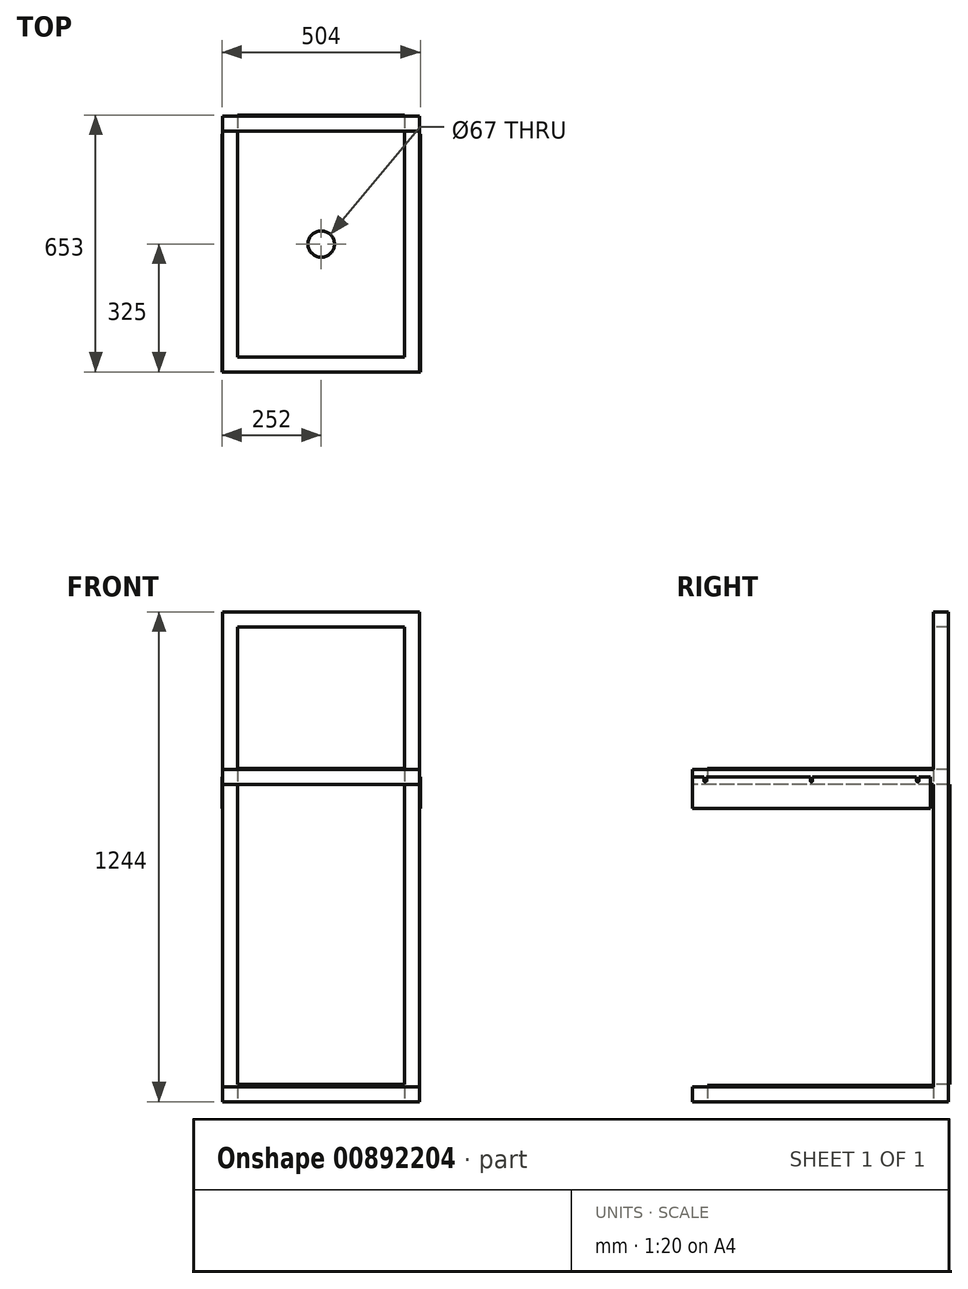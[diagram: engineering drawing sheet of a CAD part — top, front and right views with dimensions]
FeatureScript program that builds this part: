
annotation { "Feature Type Name" : "Feature", "Feature Type Description" : "" }
export const myFeature = defineFeature(function(context is Context, id is Id, definition is map)
    precondition{}
    {
        {
            var Q0;
            Q0=qCreatedBy(makeId("Front.planeOp"),FACE);
            var sketch = newSketch(context, id + "F0", { "sketchPlane" : qUnion([Q0])});
            skLineSegment(sketch, "E0.bottom", {"start": v(0, 0) * mm, "end": v(-500, 0) * mm});
            skLineSegment(sketch, "E0.top", {"start": v(0, 38) * mm, "end": v(-500, 38) * mm});
            skLineSegment(sketch, "E0.left", {"start": v(0, 0) * mm, "end": v(0, 38) * mm});
            skLineSegment(sketch, "E0.right", {"start": v(-500, 0) * mm, "end": v(-500, 38) * mm});
            skSolve(sketch);
        }
        {
            var Q0;
            Q0=makeQuery(id+"F0.imprint","IMPRINT",FACE,{"disambiguationData":[TD([[makeQuery(id+"F0.imprint","IMPRINT",EDGE,{"derivedFrom":sQuery(id+"F0.wireOp",EDGE,"E0.bottom")}),-1.0]])]});
            extrude(context, id + "F1", {"entities" : qUnion([Q0]), "oppositeDirection" : true, "depth" : 650 * mm, "offsetDistance" : 25 * mm});
        }
        {
            var Q0;
            Q0=makeQuery(id+"F1.opExtrude","SWEPT_FACE",FACE,{"disambiguationData":[OSD([sQuery(id+"F0.wireOp",EDGE,"E0.right")])]});
            var sketch = newSketch(context, id + "F2", { "sketchPlane" : qUnion([Q0])});
            skLineSegment(sketch, "E1.bottom", {"start": v(-650, 38) * mm, "end": v(-612, 38) * mm});
            skLineSegment(sketch, "E1.top", {"start": v(-650, -806) * mm, "end": v(-612, -806) * mm});
            skLineSegment(sketch, "E1.left", {"start": v(-650, 38) * mm, "end": v(-650, -806) * mm});
            skLineSegment(sketch, "E1.right", {"start": v(-612, 38) * mm, "end": v(-612, -806) * mm});
            skSolve(sketch);
        }
        {
            var Q0;
            {var subQ0=sQuery(id+"F2.wireOp",EDGE,"E1.top");Q0=makeQuery(id+"F2.imprint","IMPRINT",FACE,{"disambiguationData":[TD([[makeQuery(id+"F2.imprint","IMPRINT",EDGE,{"derivedFrom":subQ0}),1.0]])]});}
            extrude(context, id + "F3", {"entities" : qUnion([Q0]), "operationType" : NewBodyOperationType.ADD, "oppositeDirection" : true, "depth" : 500 * mm, "offsetDistance" : 25 * mm});
        }
        {
            var Q0;
            {var subQ0=sQuery(id+"F0.wireOp",EDGE,"E0.right");Q0=makeQuery(id+"F3.boolean.opBoolean","MERGE",FACE,{"derivedFrom":[makeQuery(id+"F1.opExtrude","SWEPT_FACE",FACE,{"disambiguationData":[OSD([subQ0])]}),makeQuery(id+"F3.opExtrude","CAP_FACE",FACE,{"disambiguationData":[OSD([sQuery(id+"F0.wireOp",EDGE,"E0.bottom"),subQ0,sQuery(id+"F2.wireOp",EDGE,"E1.top"),sQuery(id+"F2.wireOp",EDGE,"E1.left"),sQuery(id+"F2.wireOp",EDGE,"E1.right")])],"isStart":true})]});}
            var sketch = newSketch(context, id + "F4", { "sketchPlane" : qUnion([Q0])});
            skLineSegment(sketch, "E2.bottom", {"start": v(-650, -806) * mm, "end": v(0, -806) * mm});
            skLineSegment(sketch, "E2.top", {"start": v(-650, -768) * mm, "end": v(0, -768) * mm});
            skLineSegment(sketch, "E2.left", {"start": v(-650, -806) * mm, "end": v(-650, -768) * mm});
            skLineSegment(sketch, "E2.right", {"start": v(0, -806) * mm, "end": v(0, -768) * mm});
            skSolve(sketch);
        }
        {
            var Q0;
            Q0 = qSketchRegion(id + "F4", true);
            extrude(context, id + "F5", {"entities" : qUnion([Q0]), "operationType" : NewBodyOperationType.ADD, "oppositeDirection" : true, "depth" : 500 * mm, "offsetDistance" : 25 * mm});
        }
        {
            var Q0;
            Q0=makeQuery(id+"F1.opExtrude","SWEPT_FACE",FACE,{"disambiguationData":[OSD([sQuery(id+"F0.wireOp",EDGE,"E0.top")])]});
            var sketch = newSketch(context, id + "F6", { "sketchPlane" : qUnion([Q0])});
            skLineSegment(sketch, "E3.bottom", {"start": v(-500, 650) * mm, "end": v(-462, 650) * mm});
            skLineSegment(sketch, "E3.top", {"start": v(-500, 612) * mm, "end": v(-462, 612) * mm});
            skLineSegment(sketch, "E3.left", {"start": v(-500, 650) * mm, "end": v(-500, 612) * mm});
            skLineSegment(sketch, "E3.right", {"start": v(-462, 650) * mm, "end": v(-462, 612) * mm});
            skLineSegment(sketch, "E4.bottom", {"start": v(0, 650) * mm, "end": v(-38, 650) * mm});
            skLineSegment(sketch, "E4.top", {"start": v(0, 612) * mm, "end": v(-38, 612) * mm});
            skLineSegment(sketch, "E4.left", {"start": v(0, 650) * mm, "end": v(0, 612) * mm});
            skLineSegment(sketch, "E4.right", {"start": v(-38, 650) * mm, "end": v(-38, 612) * mm});
            skSolve(sketch);
        }
        {
            var Q0;
            Q0=makeQuery(id+"F6.imprint","IMPRINT",FACE,{"disambiguationData":[TD([[makeQuery(id+"F6.imprint","IMPRINT",EDGE,{"derivedFrom":sQuery(id+"F6.wireOp",EDGE,"E3.bottom")}),1.0]])]});
            var Q1;
            Q1=makeQuery(id+"F6.imprint","IMPRINT",FACE,{"disambiguationData":[TD([[makeQuery(id+"F6.imprint","IMPRINT",EDGE,{"derivedFrom":sQuery(id+"F6.wireOp",EDGE,"E4.bottom")}),1.0]])]});
            extrude(context, id + "F7", {"entities" : qUnion([Q0, Q1]), "operationType" : NewBodyOperationType.ADD, "depth" : 400 * mm, "offsetDistance" : 25 * mm});
        }
        {
            var Q0;
            Q0=makeQuery(id+"F7.opExtrude","SWEPT_FACE",FACE,{"disambiguationData":[OSD([sQuery(id+"F6.wireOp",EDGE,"E4.right")])]});
            var sketch = newSketch(context, id + "F8", { "sketchPlane" : qUnion([Q0])});
            skLineSegment(sketch, "E5.bottom", {"start": v(-650, 438) * mm, "end": v(-612, 438) * mm});
            skLineSegment(sketch, "E5.top", {"start": v(-650, 400) * mm, "end": v(-612, 400) * mm});
            skLineSegment(sketch, "E5.left", {"start": v(-650, 438) * mm, "end": v(-650, 400) * mm});
            skLineSegment(sketch, "E5.right", {"start": v(-612, 438) * mm, "end": v(-612, 400) * mm});
            skSolve(sketch);
        }
        {
            var Q0;
            Q0=makeQuery(id+"F8.imprint","IMPRINT",FACE,{"disambiguationData":[TD([[makeQuery(id+"F8.imprint","IMPRINT",EDGE,{"derivedFrom":sQuery(id+"F8.wireOp",EDGE,"E5.bottom")}),-1.0]])]});
            extrude(context, id + "F9", {"entities" : qUnion([Q0]), "operationType" : NewBodyOperationType.ADD, "depth" : 424 * mm, "offsetDistance" : 25 * mm});
        }
        {
            var Q0;
            Q0=makeQuery(id+"F3.opExtrude","SWEPT_FACE",FACE,{"disambiguationData":[OSD([sQuery(id+"F2.wireOp",EDGE,"E1.right")])]});
            var sketch = newSketch(context, id + "F10", { "sketchPlane" : qUnion([Q0])});
            skLineSegment(sketch, "E6.right", {"start": v(-462, 0) * mm, "end": v(-462, -762) * mm});
            skLineSegment(sketch, "E7.right", {"start": v(-38, 0) * mm, "end": v(-38, -762) * mm});
            skLineSegment(sketch, "E8.bottom", {"start": v(-462, 0) * mm, "end": v(-38, 0) * mm});
            skLineSegment(sketch, "E8.top", {"start": v(-462, -762) * mm, "end": v(-38, -762) * mm});
            skSolve(sketch);
        }
        {
            var Q0;
            Q0 = qSketchRegion(id + "F10", true);
            extrude(context, id + "F11", {"entities" : qUnion([Q0]), "operationType" : NewBodyOperationType.REMOVE, "oppositeDirection" : true, "depth" : 41 * mm, "offsetDistance" : 25 * mm});
        }
        {
            var Q0;
            Q0=makeQuery(id+"F11.boolean.opBoolean","MERGE",FACE,{"derivedFrom":[makeQuery(id+"F1.opExtrude","SWEPT_FACE",FACE,{"disambiguationData":[OSD([sQuery(id+"F0.wireOp",EDGE,"E0.bottom")])]})],"fromTools":[makeQuery(id+"F11.opExtrude","SWEPT_FACE",FACE,{"disambiguationData":[OSD([sQuery(id+"F10.wireOp",EDGE,"E8.bottom")])]})]});
            var sketch = newSketch(context, id + "F12", { "sketchPlane" : qUnion([Q0])});
            skLineSegment(sketch, "E9.bottom", {"start": v(-462, -612) * mm, "end": v(-38, -612) * mm});
            skLineSegment(sketch, "E9.top", {"start": v(-462, -38) * mm, "end": v(-38, -38) * mm});
            skLineSegment(sketch, "E9.left", {"start": v(-462, -612) * mm, "end": v(-462, -38) * mm});
            skLineSegment(sketch, "E9.right", {"start": v(-38, -612) * mm, "end": v(-38, -38) * mm});
            skSolve(sketch);
        }
        {
            var Q0;
            Q0=makeQuery(id+"F12.imprint","IMPRINT",FACE,{"disambiguationData":[TD([[makeQuery(id+"F12.imprint","IMPRINT",EDGE,{"derivedFrom":sQuery(id+"F12.wireOp",EDGE,"E9.bottom")}),1.0]])]});
            extrude(context, id + "F13", {"entities" : qUnion([Q0]), "operationType" : NewBodyOperationType.REMOVE, "oppositeDirection" : true, "depth" : 38 * mm, "offsetDistance" : 25 * mm});
        }
        {
            var Q0;
            Q0=makeQuery(id+"F5.boolean.opBoolean","MERGE",FACE,{"derivedFrom":[makeQuery(id+"F3.opExtrude","SWEPT_FACE",FACE,{"disambiguationData":[OSD([sQuery(id+"F2.wireOp",EDGE,"E1.top")])]}),makeQuery(id+"F5.opExtrude","SWEPT_FACE",FACE,{"disambiguationData":[OSD([sQuery(id+"F4.wireOp",EDGE,"E2.bottom")])]})]});
            var sketch = newSketch(context, id + "F14", { "sketchPlane" : qUnion([Q0])});
            skLineSegment(sketch, "E10.bottom", {"start": v(-462, -38) * mm, "end": v(-38, -38) * mm});
            skLineSegment(sketch, "E10.top", {"start": v(-462, -612) * mm, "end": v(-38, -612) * mm});
            skLineSegment(sketch, "E10.left", {"start": v(-462, -38) * mm, "end": v(-462, -612) * mm});
            skLineSegment(sketch, "E10.right", {"start": v(-38, -38) * mm, "end": v(-38, -612) * mm});
            skSolve(sketch);
        }
        {
            var Q0;
            Q0=makeQuery(id+"F14.imprint","IMPRINT",FACE,{"disambiguationData":[TD([[makeQuery(id+"F14.imprint","IMPRINT",EDGE,{"derivedFrom":sQuery(id+"F14.wireOp",EDGE,"E10.bottom")}),-1.0]])]});
            extrude(context, id + "F15", {"entities" : qUnion([Q0]), "operationType" : NewBodyOperationType.REMOVE, "oppositeDirection" : true, "depth" : 38 * mm, "offsetDistance" : 25 * mm});
        }
        {
            var Q0;
            Q0=makeQuery(id+"F9.boolean.opBoolean","MERGE",FACE,{"derivedFrom":[makeQuery(id+"F7.boolean.opBoolean","MERGE",FACE,{"derivedFrom":[makeQuery(id+"F3.boolean.opBoolean","MERGE",FACE,{"derivedFrom":[makeQuery(id+"F1.opExtrude","CAP_FACE",FACE,{"disambiguationData":[OSD([sQuery(id+"F0.wireOp",EDGE,"E0.bottom"),sQuery(id+"F0.wireOp",EDGE,"E0.top"),sQuery(id+"F0.wireOp",EDGE,"E0.left"),sQuery(id+"F0.wireOp",EDGE,"E0.right")])],"isStart":false}),makeQuery(id+"F3.opExtrude","SWEPT_FACE",FACE,{"disambiguationData":[OSD([sQuery(id+"F2.wireOp",EDGE,"E1.left")])]})]}),makeQuery(id+"F7.opExtrude","SWEPT_FACE",FACE,{"disambiguationData":[OSD([sQuery(id+"F6.wireOp",EDGE,"E3.bottom")])]}),makeQuery(id+"F7.opExtrude","SWEPT_FACE",FACE,{"disambiguationData":[OSD([sQuery(id+"F6.wireOp",EDGE,"E4.bottom")])]})]}),makeQuery(id+"F9.opExtrude","SWEPT_FACE",FACE,{"disambiguationData":[OSD([sQuery(id+"F8.wireOp",EDGE,"E5.left")])]})]});
            var sketch = newSketch(context, id + "F16", { "sketchPlane" : qUnion([Q0])});
            skLineSegment(sketch, "E11.bottom", {"start": v(38, 0) * mm, "end": v(462, 0) * mm});
            skLineSegment(sketch, "E11.top", {"start": v(38, -762) * mm, "end": v(462, -762) * mm});
            skLineSegment(sketch, "E11.left", {"start": v(38, 0) * mm, "end": v(38, -762) * mm});
            skLineSegment(sketch, "E11.right", {"start": v(462, 0) * mm, "end": v(462, -762) * mm});
            skSolve(sketch);
        }
        {
            var Q0;
            Q0=makeQuery(id+"F16.imprint","IMPRINT",FACE,{"disambiguationData":[TD([[makeQuery(id+"F16.imprint","IMPRINT",EDGE,{"derivedFrom":sQuery(id+"F16.wireOp",EDGE,"E11.bottom")}),-1.0]])]});
            extrude(context, id + "F17", {"entities" : qUnion([Q0]), "depth" : 3 * mm, "offsetDistance" : 25 * mm});
        }
        {
            var Q0;
            {var subQ9=sQuery(id+"F0.wireOp",EDGE,"E0.left");var subQ10=sQuery(id+"F0.wireOp",EDGE,"E0.top");var subQ11=makeQuery(id+"F1.opExtrude","SWEPT_FACE",FACE,{"disambiguationData":[OSD([subQ10])]});Q0=makeQuery(id+"F13.boolean.opBoolean","SPLIT",FACE,{"disambiguationData":[TD([makeQuery(id+"F1.opExtrude","SWEPT_FACE",FACE,{"disambiguationData":[OSD([subQ9])]})])],"derivedFrom":subQ11});}
            var sketch = newSketch(context, id + "F18", { "sketchPlane" : qUnion([Q0])});
            skLineSegment(sketch, "E12.bottom", {"start": v(-462, 612) * mm, "end": v(-38, 612) * mm});
            skLineSegment(sketch, "E12.top", {"start": v(-462, 38) * mm, "end": v(-38, 38) * mm});
            skLineSegment(sketch, "E12.left", {"start": v(-462, 612) * mm, "end": v(-462, 38) * mm});
            skLineSegment(sketch, "E12.right", {"start": v(-38, 612) * mm, "end": v(-38, 38) * mm});
            skPoint(sketch, "E13.endSnap0", {"position": v(-250, 38) * mm});
            skCircle(sketch, "E14", {"center": v(-250, 325) * mm, "radius": 33.5 * mm});
            skSolve(sketch);
        }
        {
            var Q0;
            Q0=makeQuery(id+"F18.imprint","IMPRINT",FACE,{"disambiguationData":[TD([[makeQuery(id+"F18.imprint","IMPRINT",EDGE,{"derivedFrom":sQuery(id+"F18.wireOp",EDGE,"E12.bottom")}),-1.0]])]});
            extrude(context, id + "F19", {"entities" : qUnion([Q0]), "depth" : 3 * mm, "offsetDistance" : 25 * mm});
        }
        {
            var Q0;
            Q0=makeQuery(id+"F5.opExtrude","SWEPT_FACE",FACE,{"disambiguationData":[OSD([sQuery(id+"F4.wireOp",EDGE,"E2.top")])]});
            var sketch = newSketch(context, id + "F20", { "sketchPlane" : qUnion([Q0])});
            skLineSegment(sketch, "E15.bottom", {"start": v(-462, 612) * mm, "end": v(-38, 612) * mm});
            skLineSegment(sketch, "E15.top", {"start": v(-462, 38) * mm, "end": v(-38, 38) * mm});
            skLineSegment(sketch, "E15.left", {"start": v(-462, 612) * mm, "end": v(-462, 38) * mm});
            skLineSegment(sketch, "E15.right", {"start": v(-38, 612) * mm, "end": v(-38, 38) * mm});
            skSolve(sketch);
        }
        {
            var Q0;
            Q0=makeQuery(id+"F20.imprint","IMPRINT",FACE,{"disambiguationData":[TD([[makeQuery(id+"F20.imprint","IMPRINT",EDGE,{"derivedFrom":sQuery(id+"F20.wireOp",EDGE,"E15.bottom")}),-1.0]])]});
            extrude(context, id + "F21", {"entities" : qUnion([Q0]), "depth" : 3 * mm, "offsetDistance" : 25 * mm});
        }
        {
            var Q0;
            Q0=makeQuery(id+"F7.boolean.opBoolean","MERGE",FACE,{"derivedFrom":[makeQuery(id+"F5.boolean.opBoolean","MERGE",FACE,{"derivedFrom":[makeQuery(id+"F3.boolean.opBoolean","MERGE",FACE,{"derivedFrom":[makeQuery(id+"F1.opExtrude","SWEPT_FACE",FACE,{"disambiguationData":[OSD([sQuery(id+"F0.wireOp",EDGE,"E0.left")])]}),makeQuery(id+"F3.opExtrude","CAP_FACE",FACE,{"disambiguationData":[OSD([sQuery(id+"F0.wireOp",EDGE,"E0.bottom"),sQuery(id+"F0.wireOp",EDGE,"E0.right"),sQuery(id+"F2.wireOp",EDGE,"E1.top"),sQuery(id+"F2.wireOp",EDGE,"E1.left"),sQuery(id+"F2.wireOp",EDGE,"E1.right")])],"isStart":false})]}),makeQuery(id+"F5.opExtrude","CAP_FACE",FACE,{"disambiguationData":[OSD([sQuery(id+"F4.wireOp",EDGE,"E2.bottom"),sQuery(id+"F4.wireOp",EDGE,"E2.top"),sQuery(id+"F4.wireOp",EDGE,"E2.left"),sQuery(id+"F4.wireOp",EDGE,"E2.right")])],"isStart":false})]}),makeQuery(id+"F7.opExtrude","SWEPT_FACE",FACE,{"disambiguationData":[OSD([sQuery(id+"F6.wireOp",EDGE,"E4.left")])]})]});
            var sketch = newSketch(context, id + "F22", { "sketchPlane" : qUnion([Q0])});
            skLineSegment(sketch, "E16.bottom", {"start": v(0, 19) * mm, "end": v(603.83, 19) * mm});
            skLineSegment(sketch, "E17", {"start": v(603.83, 19) * mm, "end": v(603.83, -61) * mm});
            skLineSegment(sketch, "E18", {"start": v(0, 19) * mm, "end": v(0, -61) * mm});
            skLineSegment(sketch, "E19", {"start": v(0, -61) * mm, "end": v(603.83, -61) * mm});
            skArc(sketch, "E20", {"start": v(298.92, 9.5) * mm, "mid": v(301.92, 6.5) * mm, "end": v(304.92, 9.5) * mm});
            skArc(sketch, "E21", {"start": v(28.92, 9.5) * mm, "mid": v(31.92, 6.5) * mm, "end": v(34.92, 9.5) * mm});
            skArc(sketch, "E22", {"start": v(568.92, 9.5) * mm, "mid": v(571.92, 6.5) * mm, "end": v(574.92, 9.5) * mm});
            skLineSegment(sketch, "E23", {"start": v(298.92, 9.5) * mm, "end": v(298.92, 19) * mm});
            skLineSegment(sketch, "E24", {"start": v(304.92, 9.5) * mm, "end": v(304.92, 19) * mm});
            skLineSegment(sketch, "E25", {"start": v(28.92, 9.5) * mm, "end": v(28.92, 19) * mm});
            skLineSegment(sketch, "E26", {"start": v(34.92, 9.5) * mm, "end": v(34.92, 19) * mm});
            skLineSegment(sketch, "E27", {"start": v(568.92, 9.5) * mm, "end": v(568.92, 19) * mm});
            skLineSegment(sketch, "E28", {"start": v(574.92, 9.5) * mm, "end": v(574.92, 19) * mm});
            skSolve(sketch);
        }
        {
            var Q0;
            {var subQ0=sQuery(id+"F22.wireOp",EDGE,"E19");Q0=makeQuery(id+"F22.imprint","IMPRINT",FACE,{"disambiguationData":[TD([[makeQuery(id+"F22.imprint","IMPRINT",EDGE,{"derivedFrom":subQ0}),1.0]])]});}
            var Q1;
            {var subQ0=sQuery(id+"F22.wireOp",EDGE,"E16.bottom");Q1=makeQuery(id+"F22.imprint","IMPRINT",FACE,{"disambiguationData":[TD([[makeQuery(id+"F22.imprint","IMPRINT",EDGE,{"derivedFrom":subQ0}),-1.0]])]});}
            extrude(context, id + "F23", {"entities" : qUnion([Q0, Q1]), "depth" : 2 * mm, "offsetDistance" : 25 * mm});
        }
        {
            var Q0;
            {var subQ0=sQuery(id+"F0.wireOp",EDGE,"E0.right");Q0=makeQuery(id+"F7.boolean.opBoolean","MERGE",FACE,{"derivedFrom":[makeQuery(id+"F5.boolean.opBoolean","MERGE",FACE,{"derivedFrom":[makeQuery(id+"F3.boolean.opBoolean","MERGE",FACE,{"derivedFrom":[makeQuery(id+"F1.opExtrude","SWEPT_FACE",FACE,{"disambiguationData":[OSD([subQ0])]}),makeQuery(id+"F3.opExtrude","CAP_FACE",FACE,{"disambiguationData":[OSD([sQuery(id+"F0.wireOp",EDGE,"E0.bottom"),subQ0,sQuery(id+"F2.wireOp",EDGE,"E1.top"),sQuery(id+"F2.wireOp",EDGE,"E1.left"),sQuery(id+"F2.wireOp",EDGE,"E1.right")])],"isStart":true})]}),makeQuery(id+"F5.opExtrude","CAP_FACE",FACE,{"disambiguationData":[OSD([sQuery(id+"F4.wireOp",EDGE,"E2.bottom"),sQuery(id+"F4.wireOp",EDGE,"E2.top"),sQuery(id+"F4.wireOp",EDGE,"E2.left"),sQuery(id+"F4.wireOp",EDGE,"E2.right")])],"isStart":true})]}),makeQuery(id+"F7.opExtrude","SWEPT_FACE",FACE,{"disambiguationData":[OSD([sQuery(id+"F6.wireOp",EDGE,"E3.left")])]})]});}
            var sketch = newSketch(context, id + "F24", { "sketchPlane" : qUnion([Q0])});
            skLineSegment(sketch, "E29.bottom", {"start": v(0, 19) * mm, "end": v(-603.83, 19) * mm});
            skLineSegment(sketch, "E29.top", {"start": v(0, -61) * mm, "end": v(-603.83, -61) * mm});
            skLineSegment(sketch, "E29.left", {"start": v(0, 19) * mm, "end": v(0, -61) * mm});
            skLineSegment(sketch, "E29.right", {"start": v(-603.83, 19) * mm, "end": v(-603.83, -61) * mm});
            skArc(sketch, "E30", {"start": v(-304.92, 9.5) * mm, "mid": v(-301.92, 6.5) * mm, "end": v(-298.92, 9.5) * mm});
            skArc(sketch, "E31", {"start": v(-574.92, 9.5) * mm, "mid": v(-571.92, 6.5) * mm, "end": v(-568.92, 9.5) * mm});
            skArc(sketch, "E32", {"start": v(-34.92, 9.5) * mm, "mid": v(-31.92, 6.5) * mm, "end": v(-28.92, 9.5) * mm});
            skLineSegment(sketch, "E33", {"start": v(-574.92, 9.5) * mm, "end": v(-574.92, 19) * mm});
            skLineSegment(sketch, "E34", {"start": v(-568.92, 9.5) * mm, "end": v(-568.92, 19) * mm});
            skLineSegment(sketch, "E35", {"start": v(-304.92, 9.5) * mm, "end": v(-304.92, 19) * mm});
            skLineSegment(sketch, "E36", {"start": v(-298.92, 9.5) * mm, "end": v(-298.92, 19) * mm});
            skLineSegment(sketch, "E37", {"start": v(-34.92, 9.5) * mm, "end": v(-34.92, 19) * mm});
            skLineSegment(sketch, "E38", {"start": v(-28.92, 9.5) * mm, "end": v(-28.92, 19) * mm});
            skSolve(sketch);
        }
        {
            var Q0;
            {var subQ0=sQuery(id+"F24.wireOp",EDGE,"E29.top");Q0=makeQuery(id+"F24.imprint","IMPRINT",FACE,{"disambiguationData":[TD([[makeQuery(id+"F24.imprint","IMPRINT",EDGE,{"derivedFrom":subQ0}),-1.0]])]});}
            var Q1;
            {var subQ0=sQuery(id+"F24.wireOp",EDGE,"E29.bottom");Q1=makeQuery(id+"F24.imprint","IMPRINT",FACE,{"disambiguationData":[TD([[makeQuery(id+"F24.imprint","IMPRINT",EDGE,{"derivedFrom":subQ0}),1.0]])]});}
            extrude(context, id + "F25", {"entities" : qUnion([Q0, Q1]), "depth" : 2 * mm, "offsetDistance" : 25 * mm});
        }
    });
